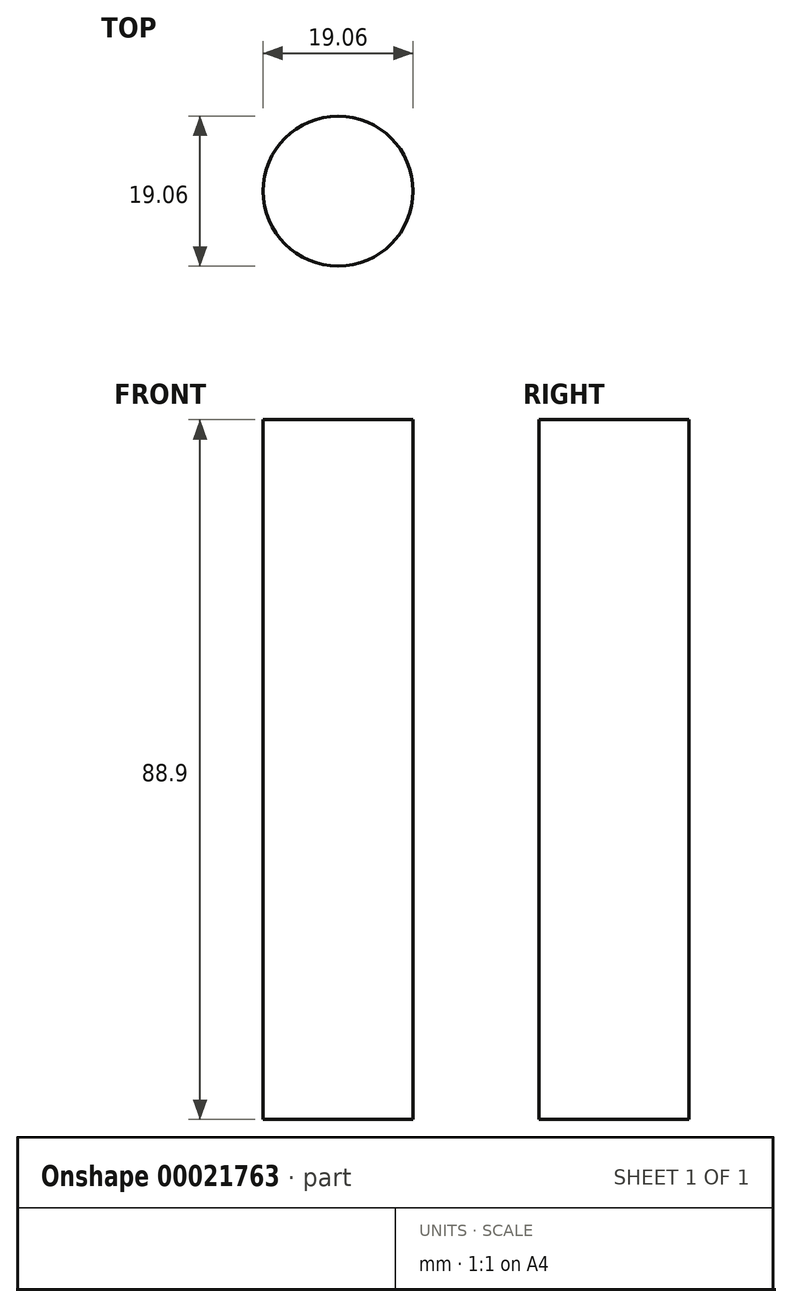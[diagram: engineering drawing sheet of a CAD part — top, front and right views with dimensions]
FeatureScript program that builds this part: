
annotation { "Feature Type Name" : "Feature", "Feature Type Description" : "" }
export const myFeature = defineFeature(function(context is Context, id is Id, definition is map)
    precondition{}
    {
        {
            var Q0;
            Q0=qCreatedBy(makeId("Front.planeOp"),FACE);
            var sketch = newSketch(context, id + "F0", { "sketchPlane" : qUnion([Q0])});
            skLineSegment(sketch, "E0.bottom", {"start": v(0, 44.33) * mm, "end": v(19.05, 44.33) * mm});
            skLineSegment(sketch, "E0.top", {"start": v(0, -44.57) * mm, "end": v(44.45, -44.57) * mm});
            skLineSegment(sketch, "E0.right", {"start": v(44.45, -25.52) * mm, "end": v(44.45, -44.57) * mm});
            skLineSegment(sketch, "E1", {"start": v(44.45, -25.52) * mm, "end": v(25.4, -25.52) * mm});
            skLineSegment(sketch, "E2", {"start": v(25.4, -25.52) * mm, "end": v(25.4, 31.63) * mm});
            skLineSegment(sketch, "E3", {"start": v(25.4, 31.63) * mm, "end": v(19.05, 31.63) * mm});
            skLineSegment(sketch, "E4", {"start": v(19.05, 31.63) * mm, "end": v(19.05, 44.33) * mm});
            skPoint(sketch, "E5.orphan", {"position": v(44.45, 44.33) * mm});
            skLineSegment(sketch, "E6", {"start": v(0, 44.33) * mm, "end": v(9.53, 44.33) * mm});
            skLineSegment(sketch, "E7", {"start": v(9.53, 44.33) * mm, "end": v(9.53, -44.57) * mm});
            skLineSegment(sketch, "E8", {"start": v(0, 44.33) * mm, "end": v(0, -44.57) * mm});
            skSolve(sketch);
        }
        {
            var Q0;
            Q0=makeQuery(id+"F0.imprint","IMPRINT",FACE,{"disambiguationData":[TD([[makeQuery(id+"F0.imprint","IMPRINT",EDGE,{"derivedFrom":sQuery(id+"F0.wireOp",EDGE,"E0.bottom")}),-1.0]])]});
            var Q1;
            Q1=sQuery(id+"F0.wireOp",EDGE,"E8");
            revolve(context, id + "F1", {"entities" : qUnion([Q0]), "axis" : qUnion([Q1]), "revolveType" : RevolveType.FULL});
        }
    });
